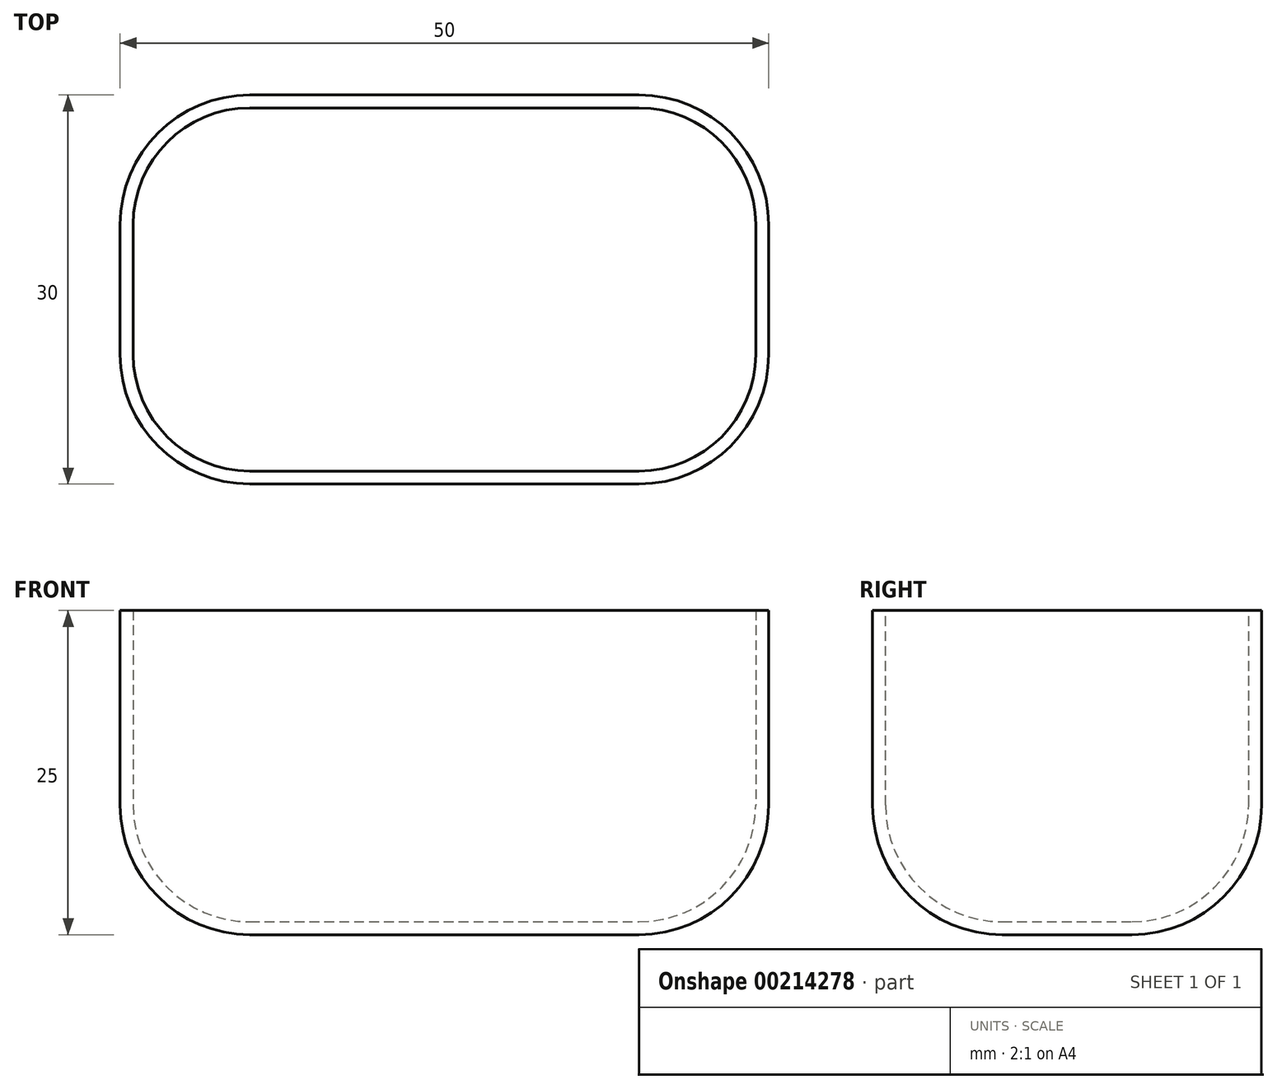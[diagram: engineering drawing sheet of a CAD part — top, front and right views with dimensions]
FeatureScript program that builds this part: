
annotation { "Feature Type Name" : "Feature", "Feature Type Description" : "" }
export const myFeature = defineFeature(function(context is Context, id is Id, definition is map)
    precondition{}
    {
        {
            var Q0;
            Q0=qCreatedBy(makeId("Top.planeOp"),FACE);
            var sketch = newSketch(context, id + "F0", { "sketchPlane" : qUnion([Q0])});
            skLineSegment(sketch, "E0.bottom", {"start": v(-25, 15) * mm, "end": v(25, 15) * mm});
            skLineSegment(sketch, "E0.top", {"start": v(-25, -15) * mm, "end": v(25, -15) * mm});
            skLineSegment(sketch, "E0.left", {"start": v(-25, 15) * mm, "end": v(-25, -15) * mm});
            skLineSegment(sketch, "E0.right", {"start": v(25, 15) * mm, "end": v(25, -15) * mm});
            skSolve(sketch);
        }
        {
            var Q0;
            Q0 = qSketchRegion(id + "F0", true);
            extrude(context, id + "F1", {"entities" : qUnion([Q0]), "depth" : 25 * mm});
        }
        {
            var Q0;
            Q0=makeQuery(id+"F1.opExtrude","SWEPT_EDGE",EDGE,{"disambiguationData":[OSD([sQuery(id+"F0.wireOp",EDGE,"E0.top"),sQuery(id+"F0.wireOp",EDGE,"E0.right")])]});
            var Q1;
            Q1=makeQuery(id+"F1.opExtrude","SWEPT_EDGE",EDGE,{"disambiguationData":[OSD([sQuery(id+"F0.wireOp",EDGE,"E0.top"),sQuery(id+"F0.wireOp",EDGE,"E0.left")])]});
            var Q2;
            Q2=makeQuery(id+"F1.opExtrude","SWEPT_EDGE",EDGE,{"disambiguationData":[OSD([sQuery(id+"F0.wireOp",EDGE,"E0.bottom"),sQuery(id+"F0.wireOp",EDGE,"E0.right")])]});
            var Q3;
            Q3=makeQuery(id+"F1.opExtrude","SWEPT_EDGE",EDGE,{"disambiguationData":[OSD([sQuery(id+"F0.wireOp",EDGE,"E0.bottom"),sQuery(id+"F0.wireOp",EDGE,"E0.left")])]});
            fillet(context, id + "F2", {"entities" : qUnion([Q0, Q1, Q2, Q3]), "radius" : 10 * mm, "tangentPropagation" : true, "allowEdgeOverflow" : false});
        }
        {
            var Q0;
            Q0=makeQuery(id+"F1.opExtrude","CAP_EDGE",EDGE,{"disambiguationData":[OSD([sQuery(id+"F0.wireOp",EDGE,"E0.top")])],"isStart":true});
            fillet(context, id + "F3", {"entities" : qUnion([Q0]), "radius" : 10 * mm, "tangentPropagation" : true, "allowEdgeOverflow" : false});
        }
        {
            var Q0;
            Q0=makeQuery(id+"F1.opExtrude","CAP_FACE",FACE,{"disambiguationData":[OSD([sQuery(id+"F0.wireOp",EDGE,"E0.bottom"),sQuery(id+"F0.wireOp",EDGE,"E0.top"),sQuery(id+"F0.wireOp",EDGE,"E0.left"),sQuery(id+"F0.wireOp",EDGE,"E0.right")])],"isStart":false});
            shell(context, id + "F4", {"entities" : qUnion([Q0]), "thickness" : 1 * mm});
        }
    });
